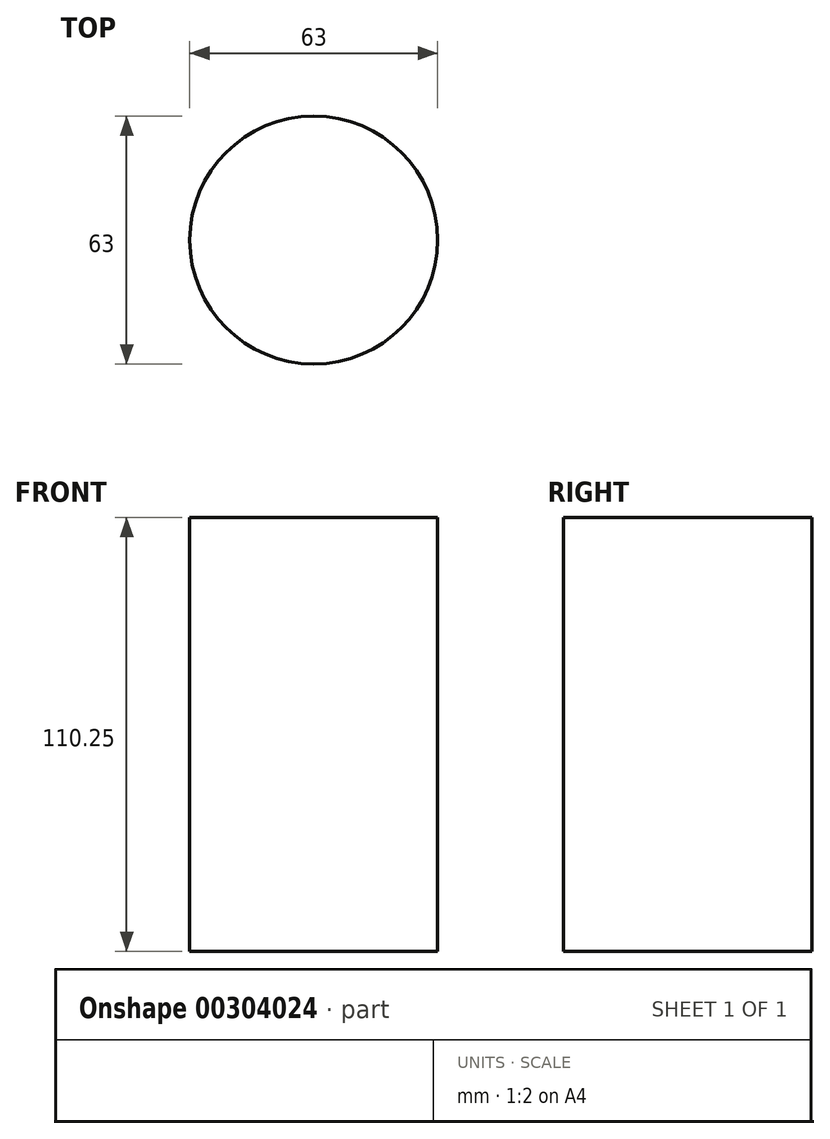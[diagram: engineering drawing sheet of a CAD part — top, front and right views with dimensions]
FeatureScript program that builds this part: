
annotation { "Feature Type Name" : "Feature", "Feature Type Description" : "" }
export const myFeature = defineFeature(function(context is Context, id is Id, definition is map)
    precondition{}
    {
        {
            var Q0;
            Q0=qCreatedBy(makeId("Front.planeOp"),FACE);
            var sketch = newSketch(context, id + "F0", { "sketchPlane" : qUnion([Q0])});
            skLineSegment(sketch, "E0", {"start": v(31.5, 55.47) * mm, "end": v(31.5, -54.78) * mm});
            skLineSegment(sketch, "E1", {"start": v(31.5, -54.78) * mm, "end": v(0, -54.78) * mm});
            skLineSegment(sketch, "E2", {"start": v(0, 55.47) * mm, "end": v(0, -54.78) * mm});
            skPoint(sketch, "E3.end.orphan", {"position": v(-30.13, 55.47) * mm});
            skLineSegment(sketch, "E4.trimOffspring", {"start": v(0, 55.47) * mm, "end": v(31.5, 55.47) * mm});
            skPoint(sketch, "E5.start.orphan", {"position": v(-30.82, 55.47) * mm});
            skSolve(sketch);
        }
        {
            var Q0;
            Q0=makeQuery(id+"F0.imprint","IMPRINT",FACE,{"disambiguationData":[TD([[makeQuery(id+"F0.imprint","IMPRINT",EDGE,{"derivedFrom":sQuery(id+"F0.wireOp",EDGE,"E0")}),-1.0]])]});
            var Q1;
            Q1=sQuery(id+"F0.wireOp",EDGE,"E2");
            revolve(context, id + "F1", {"entities" : qUnion([Q0]), "axis" : qUnion([Q1]), "revolveType" : RevolveType.FULL});
        }
    });
